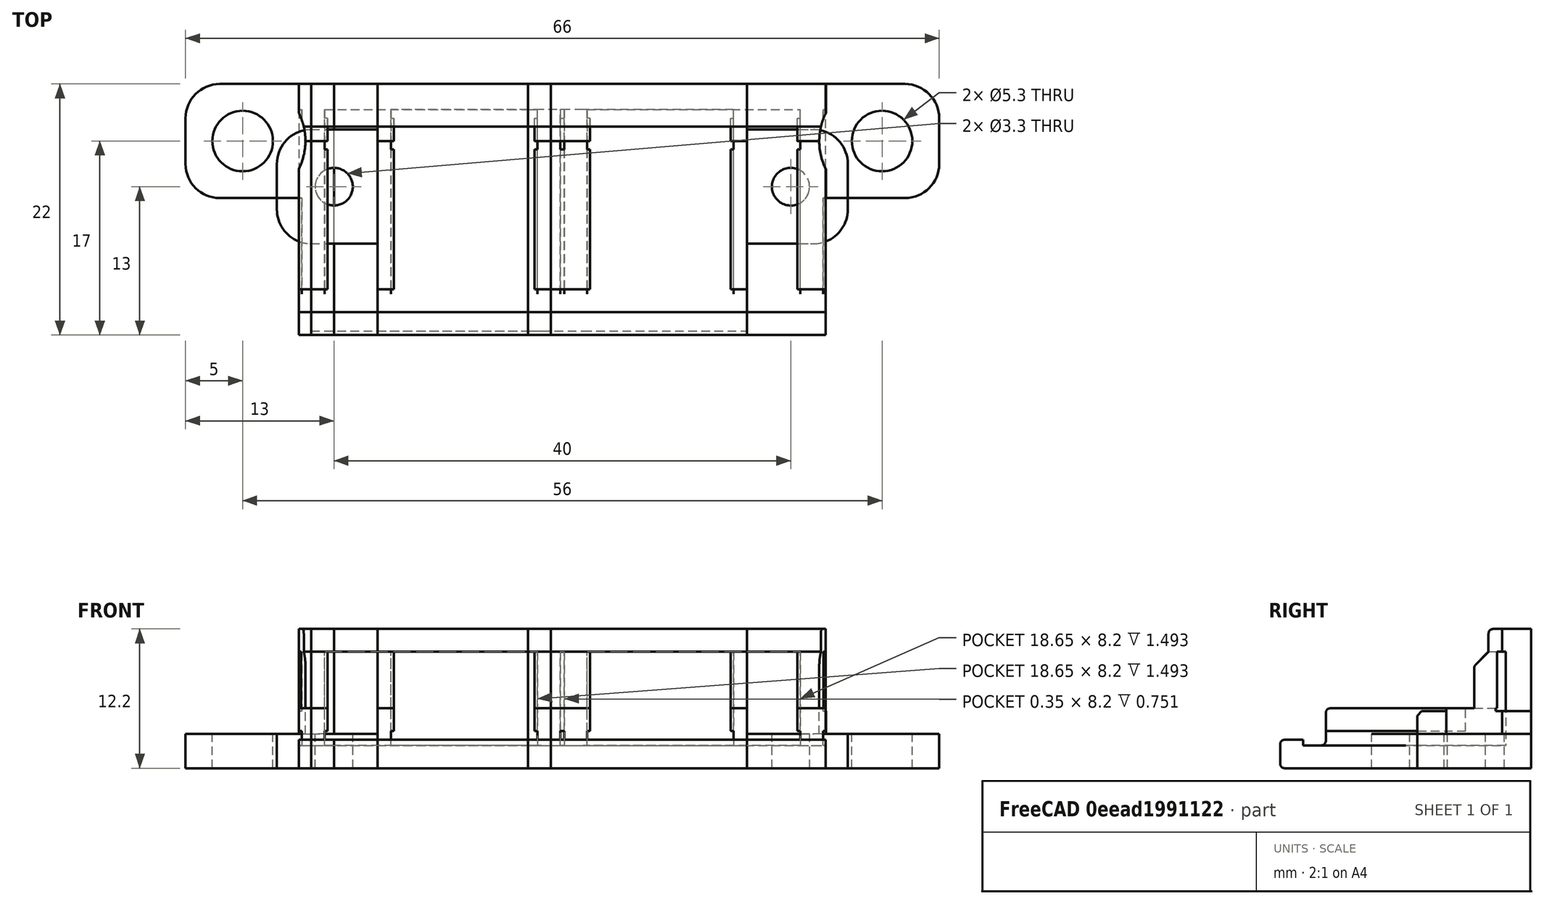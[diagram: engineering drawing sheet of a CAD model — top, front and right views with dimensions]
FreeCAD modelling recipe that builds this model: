
FCSTD DOCUMENT  (FreeCAD 0.19R24291 (Git))
Label: wago-5slot
License: Other
LicenseURL: GPL3
objects: Part::Box×11, Part::MultiFuse×9, Part::Cut×6, Part::Cylinder×6, Part::Feature×5, Part::MultiCommon×3, Part::Fillet×2
note: 42 computed .brp shape members not serialized (recipe doc carries the construction recipe); baked Part::Feature solids carry a one-line shape summary decoded from their .brp

FEATURE [Part::Feature] Cut009001  label="wago-mount"
  Placement = pos=(-2.89e-14,-1,2.17e-14) rot=(0,0,1;4.71239rad)
  shape: bbox 63.6 x 41.99 x 12.2 mm, 224 faces (baked)
FEATURE [Part::Box] Box  label="Cube"
  AttacherType = Attacher::AttachEngine3D
  Height = 15
  Length = 69
  Placement = pos=(-35,0,-1) rot=(0,0,1;0rad)
  Width = 22
FEATURE [Part::Cut] Cut
  Base = -> Cut009001
  Placement = pos=(1,0,0) rot=(0,0,1;0rad)
  Tool = -> Box
FEATURE [Part::Box] Box001  label="Cube001"
  AttacherType = Attacher::AttachEngine3D
  Height = 10
  Length = 10
  Placement = pos=(23.08,-11,0) rot=(0,0,1;0rad)
  Width = 12
FEATURE [Part::Box] Box002  label="Cube002"
  AttacherType = Attacher::AttachEngine3D
  Height = 10
  Length = 10
  Placement = pos=(-33.08,-11,0) rot=(0,0,1;0rad)
  Width = 12
FEATURE [Part::MultiFuse] Fusion
  Shapes = -> [Box001,Box002]
FEATURE [Part::Cut] Cut009002
  Base = -> Cut
  Placement = pos=(0,9,0) rot=(0,0,1;0rad)
  Tool = -> Fusion
FEATURE [Part::Box] Box003  label="Cube003"
  AttacherType = Attacher::AttachEngine3D
  Height = 3
  Length = 10
  Placement = pos=(-33,-1,0) rot=(0,0,1;0rad)
  Width = 10
FEATURE [Part::Box] Box004  label="Cube004"
  AttacherType = Attacher::AttachEngine3D
  Height = 3
  Length = 10
  Placement = pos=(23,-1,0) rot=(0,0,1;0rad)
  Width = 10
FEATURE [Part::MultiFuse] Fusion001
  Shapes = -> [Box003,Box004]
FEATURE [Part::Fillet] Fillet
  Base = -> Fusion001
  Edges = 4 edges r=3: [Edge1,Edge3,Edge17,Edge19]
FEATURE [Part::Cylinder] Cylinder
  Angle = 360
  AttacherType = Attacher::AttachEngine3D
  Height = 13
  Placement = pos=(-28,4,0) rot=(0,0,1;0rad)
  Radius = 5.5
FEATURE [Part::Cylinder] Cylinder001
  Angle = 360
  AttacherType = Attacher::AttachEngine3D
  Height = 13
  Placement = pos=(28,4,0) rot=(0,0,1;0rad)
  Radius = 5.5
FEATURE [Part::Cylinder] Cylinder002
  Angle = 360
  AttacherType = Attacher::AttachEngine3D
  Height = 15
  Placement = pos=(-28,4,0) rot=(0,0,1;0rad)
  Radius = 2.65
FEATURE [Part::Cylinder] Cylinder003
  Angle = 360
  AttacherType = Attacher::AttachEngine3D
  Height = 15
  Placement = pos=(28,4,0) rot=(0,0,1;0rad)
  Radius = 2.65
FEATURE [Part::MultiFuse] Fusion002
  Shapes = -> [Cylinder003,Cylinder002]
FEATURE [Part::MultiFuse] Fusion003
  Placement = pos=(0,0,3) rot=(0,0,1;0rad)
  Shapes = -> [Cylinder,Cylinder001]
FEATURE [Part::Cut] Cut009004
  Base = -> Fillet
  Tool = -> Fusion002
FEATURE [Part::Cut] Cut009005
  Base = -> Cut009002
  Tool = -> Fusion003
FEATURE [Part::MultiFuse] Fusion004
  Shapes = -> [Cut009005,Cut009004]
FEATURE [Part::Feature] Fusion004001
  shape: bbox 66 x 22 x 12.2 mm, 134 faces (baked)
FEATURE [Part::Box] Box005  label="Cube005"
  AttacherType = Attacher::AttachEngine3D
  Height = 14
  Length = 21
  Placement = pos=(-22,-13,0) rot=(0,0,1;0rad)
  Width = 25
FEATURE [Part::MultiCommon] Common
  Shapes = -> [Fusion004001,Box005]
FEATURE [Part::Feature] Common001
  shape: bbox 21 x 22 x 12.2 mm, 43 faces (baked)
FEATURE [Part::Feature] Common002
  shape: bbox 21 x 22 x 12.2 mm, 43 faces (baked)
FEATURE [Part::Feature] Common003
  shape: bbox 21 x 22 x 12.2 mm, 43 faces (baked)
FEATURE [Part::Box] Box006  label="Cube006"
  AttacherType = Attacher::AttachEngine3D
  Height = 14
  Length = 18
  Placement = pos=(-22,-13,0) rot=(0,0,1;0rad)
  Width = 25
FEATURE [Part::Box] Box007  label="Cube007"
  AttacherType = Attacher::AttachEngine3D
  Height = 14
  Length = 17
  Placement = pos=(-20,-13,0) rot=(0,0,1;0rad)
  Width = 25
FEATURE [Part::Box] Box008  label="Cube008"
  AttacherType = Attacher::AttachEngine3D
  Height = 14
  Length = 18
  Placement = pos=(-19,-13,0) rot=(0,0,1;0rad)
  Width = 25
FEATURE [Part::MultiCommon] Common004
  Placement = pos=(11.35,0,0) rot=(0,0,1;0rad)
  Shapes = -> [Box008,Common003]
FEATURE [Part::MultiCommon] Common005
  Shapes = -> [Box006,Common002]
FEATURE [Part::Cut] Cut009006
  Base = -> Common001
  Tool = -> Box007
FEATURE [Part::MultiFuse] Fusion004002
  Placement = pos=(5.825,0,0) rot=(0,0,1;0rad)
  Shapes = -> [Common004,Common005]
FEATURE [Part::Box] Box009  label="Cube009"
  AttacherType = Attacher::AttachEngine3D
  Height = 3
  Length = 9
  Placement = pos=(16,-5,0) rot=(0,0,1;0rad)
  Width = 10
FEATURE [Part::Box] Box010  label="Cube010"
  AttacherType = Attacher::AttachEngine3D
  Height = 3
  Length = 9
  Placement = pos=(-25,-5,0) rot=(0,0,1;0rad)
  Width = 10
FEATURE [Part::Cylinder] Cylinder004
  Angle = 360
  AttacherType = Attacher::AttachEngine3D
  Height = 10
  Placement = pos=(-20,0,0) rot=(0,0,1;0rad)
  Radius = 1.65
FEATURE [Part::Cylinder] Cylinder005
  Angle = 360
  AttacherType = Attacher::AttachEngine3D
  Height = 10
  Placement = pos=(20,0,0) rot=(0,0,1;0rad)
  Radius = 1.65
FEATURE [Part::MultiFuse] Fusion004003
  Shapes = -> [Box010,Box009]
FEATURE [Part::Fillet] Fillet001
  Base = -> Fusion004003
  Edges = 4 edges r=3: [Edge1,Edge3,Edge17,Edge19]
FEATURE [Part::MultiFuse] Fusion004004
  Shapes = -> [Cylinder004,Cylinder005]
FEATURE [Part::Cut] Cut009007
  Base = -> Fillet001
  Tool = -> Fusion004004
FEATURE [Part::MultiFuse] Fusion004005
  Shapes = -> [Fusion004002,Cut009007]
